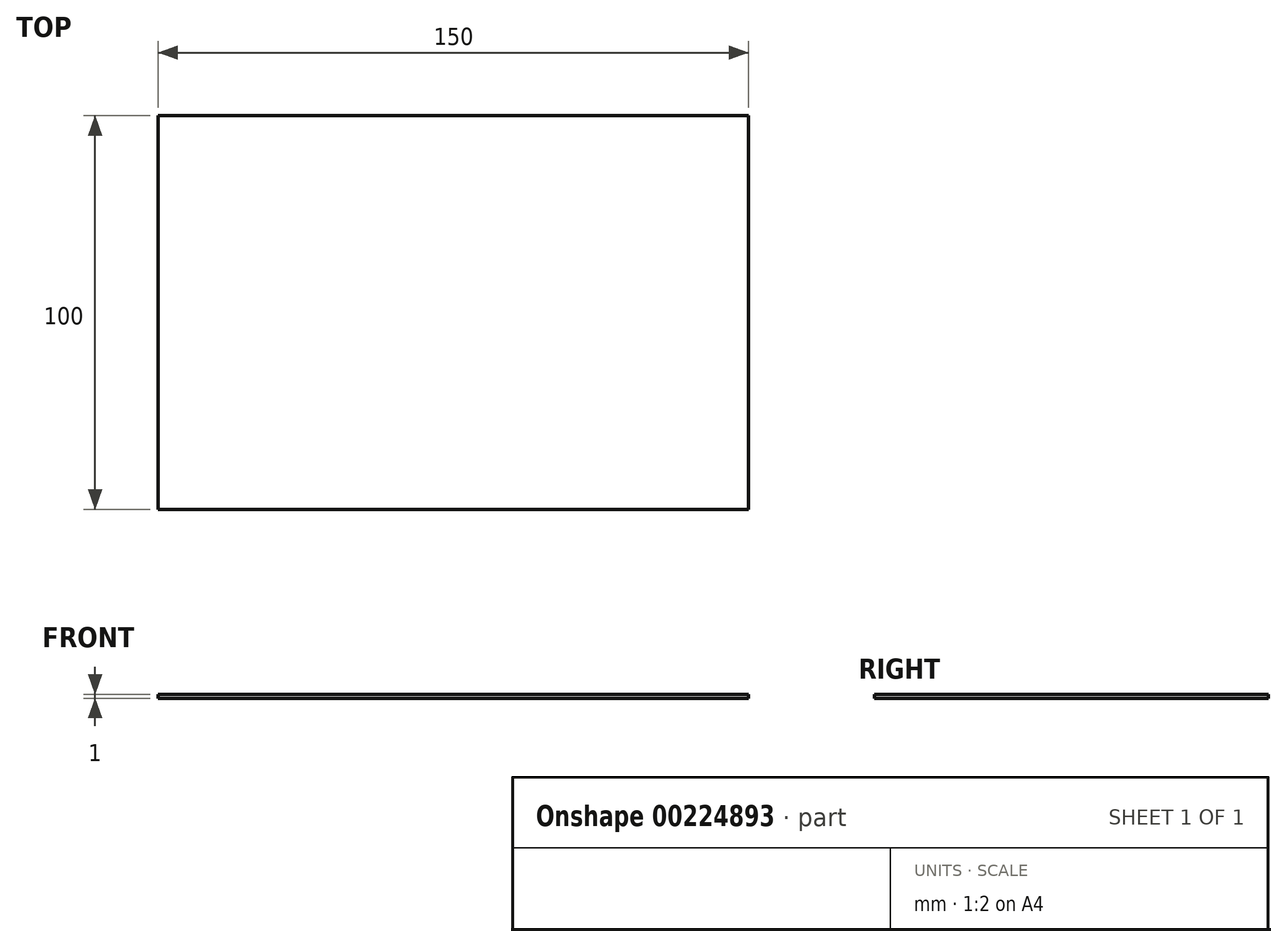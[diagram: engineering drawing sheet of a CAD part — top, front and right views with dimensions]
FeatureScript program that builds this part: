
annotation { "Feature Type Name" : "Feature", "Feature Type Description" : "" }
export const myFeature = defineFeature(function(context is Context, id is Id, definition is map)
    precondition{}
    {
        {
            var Q0;
            Q0=qCreatedBy(makeId("Top.planeOp"),FACE);
            var sketch = newSketch(context, id + "F0", { "sketchPlane" : qUnion([Q0])});
            skLineSegment(sketch, "E0.bottom", {"start": v(75, 50) * mm, "end": v(-75, 50) * mm});
            skLineSegment(sketch, "E0.top", {"start": v(75, -50) * mm, "end": v(-75, -50) * mm});
            skLineSegment(sketch, "E0.left", {"start": v(75, 50) * mm, "end": v(75, -50) * mm});
            skLineSegment(sketch, "E0.right", {"start": v(-75, 50) * mm, "end": v(-75, -50) * mm});
            skPoint(sketch, "E0.middle", {"position": v(0, 0) * mm});
            skSolve(sketch);
        }
        {
            var Q0;
            Q0=qSketchRegion(id+"F0",true);
            extrude(context, id + "F1", {"entities" : qUnion([Q0]), "depth" : 1 * mm});
        }
    });
